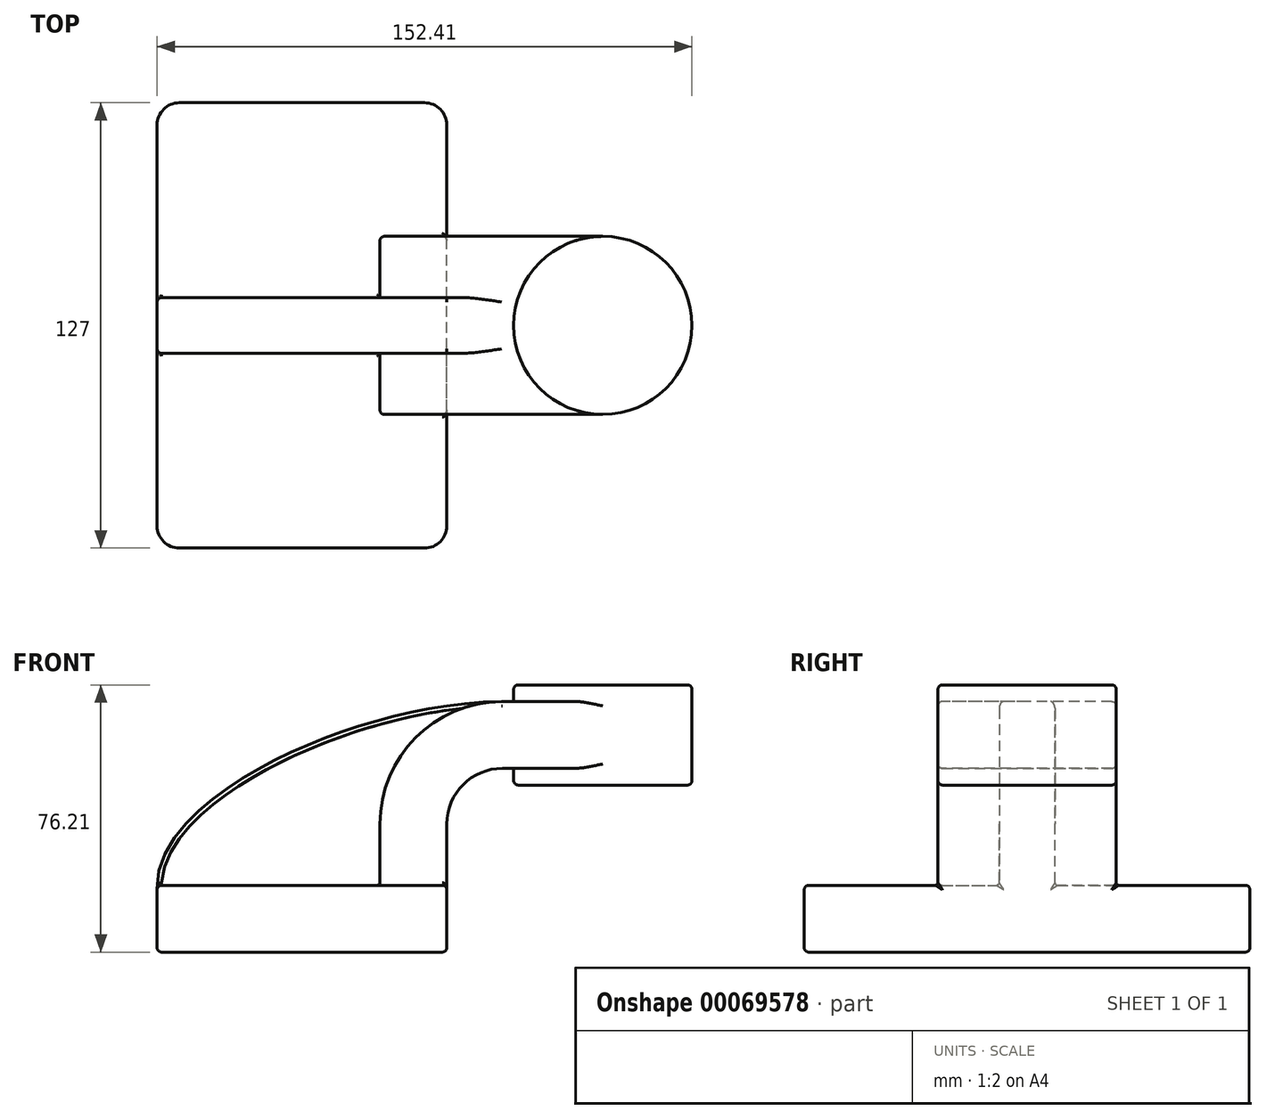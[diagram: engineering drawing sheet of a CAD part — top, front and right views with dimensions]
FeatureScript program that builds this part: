
annotation { "Feature Type Name" : "Feature", "Feature Type Description" : "" }
export const myFeature = defineFeature(function(context is Context, id is Id, definition is map)
    precondition{}
    {
        {
            var Q0;
            Q0=qCreatedBy(makeId("Front.planeOp"),FACE);
            var sketch = newSketch(context, id + "F0", { "sketchPlane" : qUnion([Q0])});
            skLineSegment(sketch, "E0.rect.bottom", {"start": v(-41.28, 9.52) * mm, "end": v(41.27, 9.53) * mm});
            skLineSegment(sketch, "E0.rect.top", {"start": v(-41.28, -9.53) * mm, "end": v(41.28, -9.53) * mm});
            skLineSegment(sketch, "E0.rect.left", {"start": v(-41.28, 9.52) * mm, "end": v(-41.27, -9.53) * mm});
            skLineSegment(sketch, "E0.rect.right", {"start": v(41.28, 9.53) * mm, "end": v(41.28, -9.52) * mm});
            skPoint(sketch, "E0.rect.middle", {"position": v(0, 0) * mm});
            skPoint(sketch, "E1.rect.middle", {"position": v(85.72, 42.88) * mm});
            skLineSegment(sketch, "E2", {"start": v(41.27, 9.53) * mm, "end": v(41.27, 27) * mm});
            skArc(sketch, "E3", {"start": v(41.27, 27) * mm, "mid": v(45.92, 38.23) * mm, "end": v(57.15, 42.88) * mm});
            skLineSegment(sketch, "E4", {"start": v(57.15, 42.88) * mm, "end": v(85.72, 42.88) * mm});
            skLineSegment(sketch, "E5.rect.bottom", {"start": v(60.32, 66.67) * mm, "end": v(111.12, 66.67) * mm});
            skLineSegment(sketch, "E5.rect.top", {"start": v(60.33, 38.1) * mm, "end": v(111.12, 38.1) * mm});
            skLineSegment(sketch, "E5.rect.left", {"start": v(60.32, 66.67) * mm, "end": v(60.33, 38.1) * mm});
            skLineSegment(sketch, "E5.rect.right", {"start": v(111.12, 66.67) * mm, "end": v(111.12, 38.1) * mm});
            skPoint(sketch, "E5.rect.middle", {"position": v(85.72, 52.39) * mm});
            skLineSegment(sketch, "E6.0", {"start": v(57.15, 61.93) * mm, "end": v(85.72, 61.93) * mm});
            skArc(sketch, "E6.1", {"start": v(22.23, 27) * mm, "mid": v(32.45, 51.7) * mm, "end": v(57.15, 61.93) * mm});
            skLineSegment(sketch, "E6.2", {"start": v(22.22, 9.53) * mm, "end": v(22.22, 27) * mm});
            skLineSegment(sketch, "E7", {"start": v(85.72, 38.1) * mm, "end": v(85.72, 66.67) * mm});
            skFitSpline(sketch, "E8", {"points": [v(-41.28, 9.52) * mm, v(57.15, 61.93) * mm], "startDerivative": vector(-0.43, 76.82) * mm, "endDerivative": vector(123.37, 0.35) * mm});
            skSolve(sketch);
        }
        {
            var Q0;
            Q0=makeQuery(id+"F0.imprint","IMPRINT",FACE,{"disambiguationData":[TD([[makeQuery(id+"F0.imprint","IMPRINT",EDGE,{"derivedFrom":sQuery(id+"F0.wireOp",EDGE,"E0.rect.top")}),1.0]])]});
            extrude(context, id + "F1", {"entities" : qUnion([Q0]), "endBound" : BoundingType.SYMMETRIC, "depth" : 127 * mm});
        }
        {
            var Q0;
            {var subQ9=sQuery(id+"F0.wireOp",EDGE,"E2");Q0=makeQuery(id+"F0.imprint","IMPRINT",FACE,{"disambiguationData":[TD([[makeQuery(id+"F0.imprint","IMPRINT",EDGE,{"derivedFrom":subQ9}),1.0]])]});}
            var Q1;
            {var subQ0=sQuery(id+"F0.wireOp",EDGE,"E7");var subQ1=sQuery(id+"F0.wireOp",EDGE,"E4");var subQ2=makeQuery(id+"F0.imprint","INTERSECT",VERTEX,{"derivedFrom":[subQ1,subQ0]});Q1=makeQuery(id+"F0.imprint","IMPRINT",FACE,{"disambiguationData":[TD([[makeQuery(id+"F0.imprint","IMPRINT",EDGE,{"disambiguationData":[TD([[subQ2,1.0]])],"derivedFrom":subQ1}),1.0]])]});}
            extrude(context, id + "F2", {"entities" : qUnion([Q0, Q1]), "operationType" : NewBodyOperationType.ADD, "endBound" : BoundingType.SYMMETRIC, "depth" : 50.8 * mm});
        }
        {
            var Q0;
            {var subQ3=sQuery(id+"F0.wireOp",EDGE,"E6.2");Q0=makeQuery(id+"F0.imprint","IMPRINT",FACE,{"disambiguationData":[TD([[makeQuery(id+"F0.imprint","IMPRINT",EDGE,{"derivedFrom":subQ3}),1.0]])]});}
            extrude(context, id + "F3", {"entities" : qUnion([Q0]), "operationType" : NewBodyOperationType.ADD, "endBound" : BoundingType.SYMMETRIC, "depth" : 15.88 * mm});
        }
        {
            var Q0;
            {var subQ5=sQuery(id+"F0.wireOp",EDGE,"E5.rect.right");Q0=makeQuery(id+"F0.imprint","IMPRINT",FACE,{"disambiguationData":[TD([[makeQuery(id+"F0.imprint","IMPRINT",EDGE,{"derivedFrom":subQ5}),-1.0]])]});}
            var Q1;
            Q1=sQuery(id+"F0.wireOp",EDGE,"E7");
            revolve(context, id + "F4", {"operationType" : NewBodyOperationType.ADD, "entities" : qUnion([Q0]), "axis" : qUnion([Q1]), "revolveType" : RevolveType.FULL});
        }
        {
            var Q0;
            Q0=makeQuery(id+"F1.opExtrude","CAP_EDGE",EDGE,{"disambiguationData":[OSD([sQuery(id+"F0.wireOp",EDGE,"E0.rect.left")])],"isStart":false});
            var Q1;
            Q1=makeQuery(id+"F1.opExtrude","CAP_EDGE",EDGE,{"disambiguationData":[OSD([sQuery(id+"F0.wireOp",EDGE,"E0.rect.left")])],"isStart":true});
            var Q2;
            Q2=makeQuery(id+"F1.opExtrude","CAP_EDGE",EDGE,{"disambiguationData":[OSD([sQuery(id+"F0.wireOp",EDGE,"E0.rect.right")])],"isStart":false});
            var Q3;
            Q3=makeQuery(id+"F1.opExtrude","CAP_EDGE",EDGE,{"disambiguationData":[OSD([sQuery(id+"F0.wireOp",EDGE,"E0.rect.right")])],"isStart":true});
            fillet(context, id + "F5", {"entities" : qUnion([Q0, Q1, Q2, Q3]), "radius" : 6.35 * mm, "tangentPropagation" : true, "allowEdgeOverflow" : false});
        }
        {
            var Q0;
            Q0=makeQuery(id+"F3.opExtrude","CAP_EDGE",EDGE,{"disambiguationData":[OSD([sQuery(id+"F0.wireOp",EDGE,"E8")])],"isStart":false});
            var Q1;
            Q1=makeQuery(id+"F3.opExtrude","CAP_EDGE",EDGE,{"disambiguationData":[OSD([sQuery(id+"F0.wireOp",EDGE,"E8")])],"isStart":true});
            fillet(context, id + "F6", {"entities" : qUnion([Q0, Q1]), "radius" : 1.27 * mm, "tangentPropagation" : true, "allowEdgeOverflow" : false});
        }
        {
            var Q0;
            Q0=makeQuery(id+"F2.opExtrude","CAP_EDGE",EDGE,{"disambiguationData":[OSD([sQuery(id+"F0.wireOp",EDGE,"E6.0")])],"isStart":false});
            var Q1;
            Q1=makeQuery(id+"F2.opExtrude","CAP_EDGE",EDGE,{"disambiguationData":[OSD([sQuery(id+"F0.wireOp",EDGE,"E6.1")])],"isStart":false});
            var Q2;
            Q2=makeQuery(id+"F2.opExtrude","CAP_EDGE",EDGE,{"disambiguationData":[OSD([sQuery(id+"F0.wireOp",EDGE,"E6.2")])],"isStart":false});
            var Q3;
            {var subQ0=sQuery(id+"F0.wireOp",EDGE,"E2");var subQ1=sQuery(id+"F0.wireOp",EDGE,"E0.rect.bottom");var subQ2=sQuery(id+"F0.wireOp",EDGE,"E0.rect.right");Q3=makeQuery(id+"F2.boolean.opBoolean","SPLIT",EDGE,{"disambiguationData":[TD([makeQuery(id+"F1.opExtrude","CAP_FACE",FACE,{"disambiguationData":[OSD([subQ1,sQuery(id+"F0.wireOp",EDGE,"E0.rect.top"),sQuery(id+"F0.wireOp",EDGE,"E0.rect.left"),subQ2])],"isStart":false})])],"derivedFrom":makeQuery(id+"F1.opExtrude","SWEPT_EDGE",EDGE,{"disambiguationData":[OSD([subQ1,subQ2,subQ0])]})});}
            var Q4;
            {var subQ4=sQuery(id+"F0.wireOp",EDGE,"E0.rect.bottom");var subQ5=sQuery(id+"F0.wireOp",EDGE,"E0.rect.right");var subQ6=sQuery(id+"F0.wireOp",EDGE,"E0.rect.left");Q4=makeQuery(id+"F5.opFillet","BLEND_EDGE",EDGE,{"blendedFrom":[makeQuery(id+"F1.opExtrude","CAP_EDGE",EDGE,{"disambiguationData":[OSD([subQ5])],"isStart":false}),makeQuery(id+"F3.boolean.opBoolean","SPLIT",FACE,{"disambiguationData":[TD([makeQuery(id+"F1.opExtrude","CAP_FACE",FACE,{"disambiguationData":[OSD([subQ4,sQuery(id+"F0.wireOp",EDGE,"E0.rect.top"),subQ6,subQ5])],"isStart":false})])],"derivedFrom":makeQuery(id+"F1.opExtrude","SWEPT_FACE",FACE,{"disambiguationData":[OSD([subQ4])]})})],"blendedInto":[makeQuery(id+"F3.boolean.opBoolean","SPLIT",FACE,{"disambiguationData":[TD([makeQuery(id+"F1.opExtrude","CAP_FACE",FACE,{"disambiguationData":[OSD([subQ4,sQuery(id+"F0.wireOp",EDGE,"E0.rect.top"),subQ6,subQ5])],"isStart":false})])],"derivedFrom":makeQuery(id+"F1.opExtrude","SWEPT_FACE",FACE,{"disambiguationData":[OSD([subQ4])]})})]});}
            var Q5;
            Q5=makeQuery(id+"F1.opExtrude","CAP_EDGE",EDGE,{"disambiguationData":[OSD([sQuery(id+"F0.wireOp",EDGE,"E0.rect.bottom")])],"isStart":false});
            var Q6;
            {var subQ4=sQuery(id+"F0.wireOp",EDGE,"E0.rect.bottom");var subQ5=sQuery(id+"F0.wireOp",EDGE,"E0.rect.right");var subQ6=sQuery(id+"F0.wireOp",EDGE,"E0.rect.left");Q6=makeQuery(id+"F5.opFillet","BLEND_EDGE",EDGE,{"blendedFrom":[makeQuery(id+"F1.opExtrude","CAP_EDGE",EDGE,{"disambiguationData":[OSD([subQ6])],"isStart":false}),makeQuery(id+"F3.boolean.opBoolean","SPLIT",FACE,{"disambiguationData":[TD([makeQuery(id+"F1.opExtrude","CAP_FACE",FACE,{"disambiguationData":[OSD([subQ4,sQuery(id+"F0.wireOp",EDGE,"E0.rect.top"),subQ6,subQ5])],"isStart":false})])],"derivedFrom":makeQuery(id+"F1.opExtrude","SWEPT_FACE",FACE,{"disambiguationData":[OSD([subQ4])]})})],"blendedInto":[makeQuery(id+"F3.boolean.opBoolean","SPLIT",FACE,{"disambiguationData":[TD([makeQuery(id+"F1.opExtrude","CAP_FACE",FACE,{"disambiguationData":[OSD([subQ4,sQuery(id+"F0.wireOp",EDGE,"E0.rect.top"),subQ6,subQ5])],"isStart":false})])],"derivedFrom":makeQuery(id+"F1.opExtrude","SWEPT_FACE",FACE,{"disambiguationData":[OSD([subQ4])]})})]});}
            var Q7;
            {var subQ0=sQuery(id+"F0.wireOp",EDGE,"E8");var subQ1=sQuery(id+"F0.wireOp",EDGE,"E0.rect.left");var subQ2=sQuery(id+"F0.wireOp",EDGE,"E0.rect.bottom");Q7=makeQuery(id+"F3.boolean.opBoolean","SPLIT",EDGE,{"disambiguationData":[TD([makeQuery(id+"F1.opExtrude","CAP_FACE",FACE,{"disambiguationData":[OSD([subQ2,sQuery(id+"F0.wireOp",EDGE,"E0.rect.top"),subQ1,sQuery(id+"F0.wireOp",EDGE,"E0.rect.right")])],"isStart":false})])],"derivedFrom":makeQuery(id+"F1.opExtrude","SWEPT_EDGE",EDGE,{"disambiguationData":[OSD([subQ2,subQ1,subQ0])]})});}
            fillet(context, id + "F7", {"entities" : qUnion([Q0, Q1, Q2, Q3, Q4, Q5, Q6, Q7]), "radius" : 1.27 * mm, "tangentPropagation" : true, "allowEdgeOverflow" : false});
        }
        {
            var Q0;
            {var subQ4=sQuery(id+"F0.wireOp",EDGE,"E0.rect.bottom");var subQ5=sQuery(id+"F0.wireOp",EDGE,"E0.rect.right");var subQ6=sQuery(id+"F0.wireOp",EDGE,"E0.rect.left");Q0=makeQuery(id+"F5.opFillet","BLEND_EDGE",EDGE,{"blendedFrom":[makeQuery(id+"F1.opExtrude","CAP_EDGE",EDGE,{"disambiguationData":[OSD([subQ6])],"isStart":true}),makeQuery(id+"F3.boolean.opBoolean","SPLIT",FACE,{"disambiguationData":[TD([makeQuery(id+"F1.opExtrude","CAP_FACE",FACE,{"disambiguationData":[OSD([subQ4,sQuery(id+"F0.wireOp",EDGE,"E0.rect.top"),subQ6,subQ5])],"isStart":true})])],"derivedFrom":makeQuery(id+"F1.opExtrude","SWEPT_FACE",FACE,{"disambiguationData":[OSD([subQ4])]})})],"blendedInto":[makeQuery(id+"F3.boolean.opBoolean","SPLIT",FACE,{"disambiguationData":[TD([makeQuery(id+"F1.opExtrude","CAP_FACE",FACE,{"disambiguationData":[OSD([subQ4,sQuery(id+"F0.wireOp",EDGE,"E0.rect.top"),subQ6,subQ5])],"isStart":true})])],"derivedFrom":makeQuery(id+"F1.opExtrude","SWEPT_FACE",FACE,{"disambiguationData":[OSD([subQ4])]})})]});}
            var Q1;
            Q1=makeQuery(id+"F1.opExtrude","CAP_EDGE",EDGE,{"disambiguationData":[OSD([sQuery(id+"F0.wireOp",EDGE,"E0.rect.bottom")])],"isStart":true});
            var Q2;
            {var subQ4=sQuery(id+"F0.wireOp",EDGE,"E0.rect.bottom");var subQ5=sQuery(id+"F0.wireOp",EDGE,"E0.rect.right");var subQ6=sQuery(id+"F0.wireOp",EDGE,"E0.rect.left");Q2=makeQuery(id+"F5.opFillet","BLEND_EDGE",EDGE,{"blendedFrom":[makeQuery(id+"F1.opExtrude","CAP_EDGE",EDGE,{"disambiguationData":[OSD([subQ5])],"isStart":true}),makeQuery(id+"F3.boolean.opBoolean","SPLIT",FACE,{"disambiguationData":[TD([makeQuery(id+"F1.opExtrude","CAP_FACE",FACE,{"disambiguationData":[OSD([subQ4,sQuery(id+"F0.wireOp",EDGE,"E0.rect.top"),subQ6,subQ5])],"isStart":true})])],"derivedFrom":makeQuery(id+"F1.opExtrude","SWEPT_FACE",FACE,{"disambiguationData":[OSD([subQ4])]})})],"blendedInto":[makeQuery(id+"F3.boolean.opBoolean","SPLIT",FACE,{"disambiguationData":[TD([makeQuery(id+"F1.opExtrude","CAP_FACE",FACE,{"disambiguationData":[OSD([subQ4,sQuery(id+"F0.wireOp",EDGE,"E0.rect.top"),subQ6,subQ5])],"isStart":true})])],"derivedFrom":makeQuery(id+"F1.opExtrude","SWEPT_FACE",FACE,{"disambiguationData":[OSD([subQ4])]})})]});}
            var Q3;
            {var subQ0=sQuery(id+"F0.wireOp",EDGE,"E2");var subQ1=sQuery(id+"F0.wireOp",EDGE,"E0.rect.bottom");var subQ2=sQuery(id+"F0.wireOp",EDGE,"E0.rect.right");Q3=makeQuery(id+"F2.boolean.opBoolean","SPLIT",EDGE,{"disambiguationData":[TD([makeQuery(id+"F1.opExtrude","CAP_FACE",FACE,{"disambiguationData":[OSD([subQ1,sQuery(id+"F0.wireOp",EDGE,"E0.rect.top"),sQuery(id+"F0.wireOp",EDGE,"E0.rect.left"),subQ2])],"isStart":true})])],"derivedFrom":makeQuery(id+"F1.opExtrude","SWEPT_EDGE",EDGE,{"disambiguationData":[OSD([subQ1,subQ2,subQ0])]})});}
            fillet(context, id + "F8", {"entities" : qUnion([Q0, Q1, Q2, Q3]), "radius" : 1.27 * mm, "tangentPropagation" : true, "allowEdgeOverflow" : false});
        }
        {
            var Q0;
            Q0=makeQuery(id+"F2.opExtrude","CAP_EDGE",EDGE,{"disambiguationData":[OSD([sQuery(id+"F0.wireOp",EDGE,"E6.0")])],"isStart":true});
            var Q1;
            Q1=makeQuery(id+"F2.opExtrude","CAP_EDGE",EDGE,{"disambiguationData":[OSD([sQuery(id+"F0.wireOp",EDGE,"E6.1")])],"isStart":true});
            var Q2;
            Q2=makeQuery(id+"F2.opExtrude","CAP_EDGE",EDGE,{"disambiguationData":[OSD([sQuery(id+"F0.wireOp",EDGE,"E6.2")])],"isStart":true});
            fillet(context, id + "F9", {"entities" : qUnion([Q0, Q1, Q2]), "radius" : 1.27 * mm, "tangentPropagation" : true, "allowEdgeOverflow" : false});
        }
        {
            var Q0;
            Q0=makeQuery(id+"F4.opRevolve","SWEPT_EDGE",EDGE,{"disambiguationData":[OSD([sQuery(id+"F0.wireOp",EDGE,"E5.rect.bottom"),sQuery(id+"F0.wireOp",EDGE,"E5.rect.right")])]});
            fillet(context, id + "F10", {"entities" : qUnion([Q0]), "radius" : 1.27 * mm, "tangentPropagation" : true, "allowEdgeOverflow" : false});
        }
        {
            var Q0;
            Q0=makeQuery(id+"F2.opExtrude","CAP_EDGE",EDGE,{"disambiguationData":[OSD([sQuery(id+"F0.wireOp",EDGE,"E4")])],"isStart":false});
            var Q1;
            Q1=makeQuery(id+"F2.opExtrude","CAP_EDGE",EDGE,{"disambiguationData":[OSD([sQuery(id+"F0.wireOp",EDGE,"E3")])],"isStart":false});
            var Q2;
            Q2=makeQuery(id+"F2.opExtrude","CAP_EDGE",EDGE,{"disambiguationData":[OSD([sQuery(id+"F0.wireOp",EDGE,"E2")])],"isStart":false});
            var Q3;
            Q3=makeQuery(id+"F2.opExtrude","CAP_EDGE",EDGE,{"disambiguationData":[OSD([sQuery(id+"F0.wireOp",EDGE,"E2")])],"isStart":true});
            var Q4;
            Q4=makeQuery(id+"F2.opExtrude","CAP_EDGE",EDGE,{"disambiguationData":[OSD([sQuery(id+"F0.wireOp",EDGE,"E3")])],"isStart":true});
            var Q5;
            Q5=makeQuery(id+"F2.opExtrude","CAP_EDGE",EDGE,{"disambiguationData":[OSD([sQuery(id+"F0.wireOp",EDGE,"E4")])],"isStart":true});
            fillet(context, id + "F11", {"entities" : qUnion([Q0, Q1, Q2, Q3, Q4, Q5]), "radius" : 1.27 * mm, "tangentPropagation" : true, "allowEdgeOverflow" : false});
        }
        {
            var Q0;
            Q0=makeQuery(id+"F4.opRevolve","SWEPT_EDGE",EDGE,{"disambiguationData":[OSD([sQuery(id+"F0.wireOp",EDGE,"E5.rect.top"),sQuery(id+"F0.wireOp",EDGE,"E5.rect.right")])]});
            fillet(context, id + "F12", {"entities" : qUnion([Q0]), "radius" : 1.27 * mm, "tangentPropagation" : true, "allowEdgeOverflow" : false});
        }
        {
            var Q0;
            Q0=makeQuery(id+"F1.opExtrude","SWEPT_FACE",FACE,{"disambiguationData":[OSD([sQuery(id+"F0.wireOp",EDGE,"E0.rect.top")])]});
            fillet(context, id + "F13", {"entities" : qUnion([Q0]), "radius" : 1.27 * mm, "tangentPropagation" : true, "allowEdgeOverflow" : false});
        }
        {
            var Q0;
            Q0=makeQuery(id+"F2.opExtrude","CAP_EDGE",EDGE,{"disambiguationData":[OSD([sQuery(id+"F0.wireOp",EDGE,"E0.rect.bottom")])],"isStart":true});
            var Q1;
            {var subQ1=sQuery(id+"F0.wireOp",EDGE,"E6.2");var subQ4=sQuery(id+"F0.wireOp",EDGE,"E0.rect.bottom");var subQ5=sQuery(id+"F0.wireOp",EDGE,"E0.rect.right");var subQ6=sQuery(id+"F0.wireOp",EDGE,"E0.rect.left");Q1=makeQuery(id+"F9.opFillet","BLEND_EDGE",EDGE,{"blendedFrom":[makeQuery(id+"F2.opExtrude","CAP_EDGE",EDGE,{"disambiguationData":[OSD([subQ1])],"isStart":true}),makeQuery(id+"F3.boolean.opBoolean","SPLIT",FACE,{"disambiguationData":[TD([makeQuery(id+"F1.opExtrude","CAP_FACE",FACE,{"disambiguationData":[OSD([subQ4,sQuery(id+"F0.wireOp",EDGE,"E0.rect.top"),subQ6,subQ5])],"isStart":true})])],"derivedFrom":makeQuery(id+"F1.opExtrude","SWEPT_FACE",FACE,{"disambiguationData":[OSD([subQ4])]})})],"blendedInto":[makeQuery(id+"F3.boolean.opBoolean","SPLIT",FACE,{"disambiguationData":[TD([makeQuery(id+"F1.opExtrude","CAP_FACE",FACE,{"disambiguationData":[OSD([subQ4,sQuery(id+"F0.wireOp",EDGE,"E0.rect.top"),subQ6,subQ5])],"isStart":true})])],"derivedFrom":makeQuery(id+"F1.opExtrude","SWEPT_FACE",FACE,{"disambiguationData":[OSD([subQ4])]})})]});}
            var Q2;
            {var subQ0=sQuery(id+"F0.wireOp",EDGE,"E0.rect.bottom");var subQ1=sQuery(id+"F0.wireOp",EDGE,"E8");var subQ2=sQuery(id+"F0.wireOp",EDGE,"E6.2");var subQ3=sQuery(id+"F0.wireOp",EDGE,"E6.1");Q2=makeQuery(id+"F3.boolean.opBoolean","SPLIT",EDGE,{"disambiguationData":[TD([makeQuery(id+"F3.opExtrude","CAP_FACE",FACE,{"disambiguationData":[OSD([subQ0,subQ3,subQ2,subQ1])],"isStart":true})])],"derivedFrom":makeQuery(id+"F2.opExtrude","SWEPT_EDGE",EDGE,{"disambiguationData":[OSD([subQ0,subQ2])]})});}
            var Q3;
            Q3=makeQuery(id+"F3.opExtrude","CAP_EDGE",EDGE,{"disambiguationData":[OSD([sQuery(id+"F0.wireOp",EDGE,"E0.rect.bottom")])],"isStart":true});
            var Q4;
            Q4=makeQuery(id+"F3.opExtrude","CAP_EDGE",EDGE,{"disambiguationData":[OSD([sQuery(id+"F0.wireOp",EDGE,"E0.rect.bottom")])],"isStart":false});
            var Q5;
            {var subQ0=sQuery(id+"F0.wireOp",EDGE,"E0.rect.bottom");var subQ1=sQuery(id+"F0.wireOp",EDGE,"E8");var subQ2=sQuery(id+"F0.wireOp",EDGE,"E6.2");var subQ3=sQuery(id+"F0.wireOp",EDGE,"E6.1");Q5=makeQuery(id+"F3.boolean.opBoolean","SPLIT",EDGE,{"disambiguationData":[TD([makeQuery(id+"F3.opExtrude","CAP_FACE",FACE,{"disambiguationData":[OSD([subQ0,subQ3,subQ2,subQ1])],"isStart":false})])],"derivedFrom":makeQuery(id+"F2.opExtrude","SWEPT_EDGE",EDGE,{"disambiguationData":[OSD([subQ0,subQ2])]})});}
            var Q6;
            {var subQ1=sQuery(id+"F0.wireOp",EDGE,"E6.2");var subQ4=sQuery(id+"F0.wireOp",EDGE,"E0.rect.bottom");var subQ5=sQuery(id+"F0.wireOp",EDGE,"E0.rect.right");var subQ6=sQuery(id+"F0.wireOp",EDGE,"E0.rect.left");Q6=makeQuery(id+"F7.opFillet","BLEND_EDGE",EDGE,{"blendedFrom":[makeQuery(id+"F2.opExtrude","CAP_EDGE",EDGE,{"disambiguationData":[OSD([subQ1])],"isStart":false}),makeQuery(id+"F3.boolean.opBoolean","SPLIT",FACE,{"disambiguationData":[TD([makeQuery(id+"F1.opExtrude","CAP_FACE",FACE,{"disambiguationData":[OSD([subQ4,sQuery(id+"F0.wireOp",EDGE,"E0.rect.top"),subQ6,subQ5])],"isStart":false})])],"derivedFrom":makeQuery(id+"F1.opExtrude","SWEPT_FACE",FACE,{"disambiguationData":[OSD([subQ4])]})})],"blendedInto":[makeQuery(id+"F3.boolean.opBoolean","SPLIT",FACE,{"disambiguationData":[TD([makeQuery(id+"F1.opExtrude","CAP_FACE",FACE,{"disambiguationData":[OSD([subQ4,sQuery(id+"F0.wireOp",EDGE,"E0.rect.top"),subQ6,subQ5])],"isStart":false})])],"derivedFrom":makeQuery(id+"F1.opExtrude","SWEPT_FACE",FACE,{"disambiguationData":[OSD([subQ4])]})})]});}
            var Q7;
            Q7=makeQuery(id+"F2.opExtrude","CAP_EDGE",EDGE,{"disambiguationData":[OSD([sQuery(id+"F0.wireOp",EDGE,"E0.rect.bottom")])],"isStart":false});
            fillet(context, id + "F14", {"entities" : qUnion([Q0, Q1, Q2, Q3, Q4, Q5, Q6, Q7]), "radius" : 0.76 * mm, "tangentPropagation" : true, "allowEdgeOverflow" : false});
        }
    });
